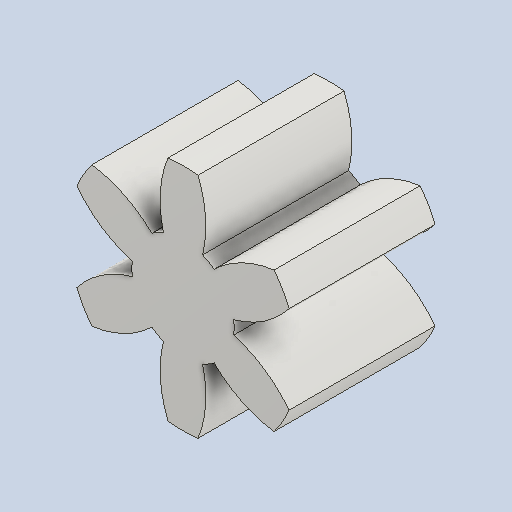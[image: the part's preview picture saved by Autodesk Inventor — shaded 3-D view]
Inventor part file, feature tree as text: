
AUTODESK INVENTOR PART (.ipt)
format: ipt  version: 2023.1 (Build 271208000, 208)  size: 182,784 bytes
history: native  units: mm (DEFAULTED — no unit token found)
features: plane x3, other x3, sketch x2, extrude x1
ambient origin geometry x8: Origin, YZ Plane, XZ Plane, XY Plane, X Axis, Y Axis, Z Axis, Center Point
bodies: Solid1 (feature_tree)
feature tree (9):
  extrude  "Extrusion1"  Depth=10.0mm TaperAngle=0.0deg
  plane  "Work Plane2"
  plane  "Work Plane8"
  plane  "Work Plane9"
  other  "Spur Gear"
  sketch  "Sketch1"  dims[d0=15.731825mm d1=10.0mm d2=0.0mm]
  sketch  "Sketch2"  dims[d3=12.0mm d4=10.0mm d5=0.0mm d16=20.0mm d17=0.0mm d34=30.0deg d39=0.0mm d41=0.0mm d43=20.0mm d46=20.0mm d47=0.0mm d48=0.0mm]
  other  "Srf1"
  other  "Pitch Diameter"
